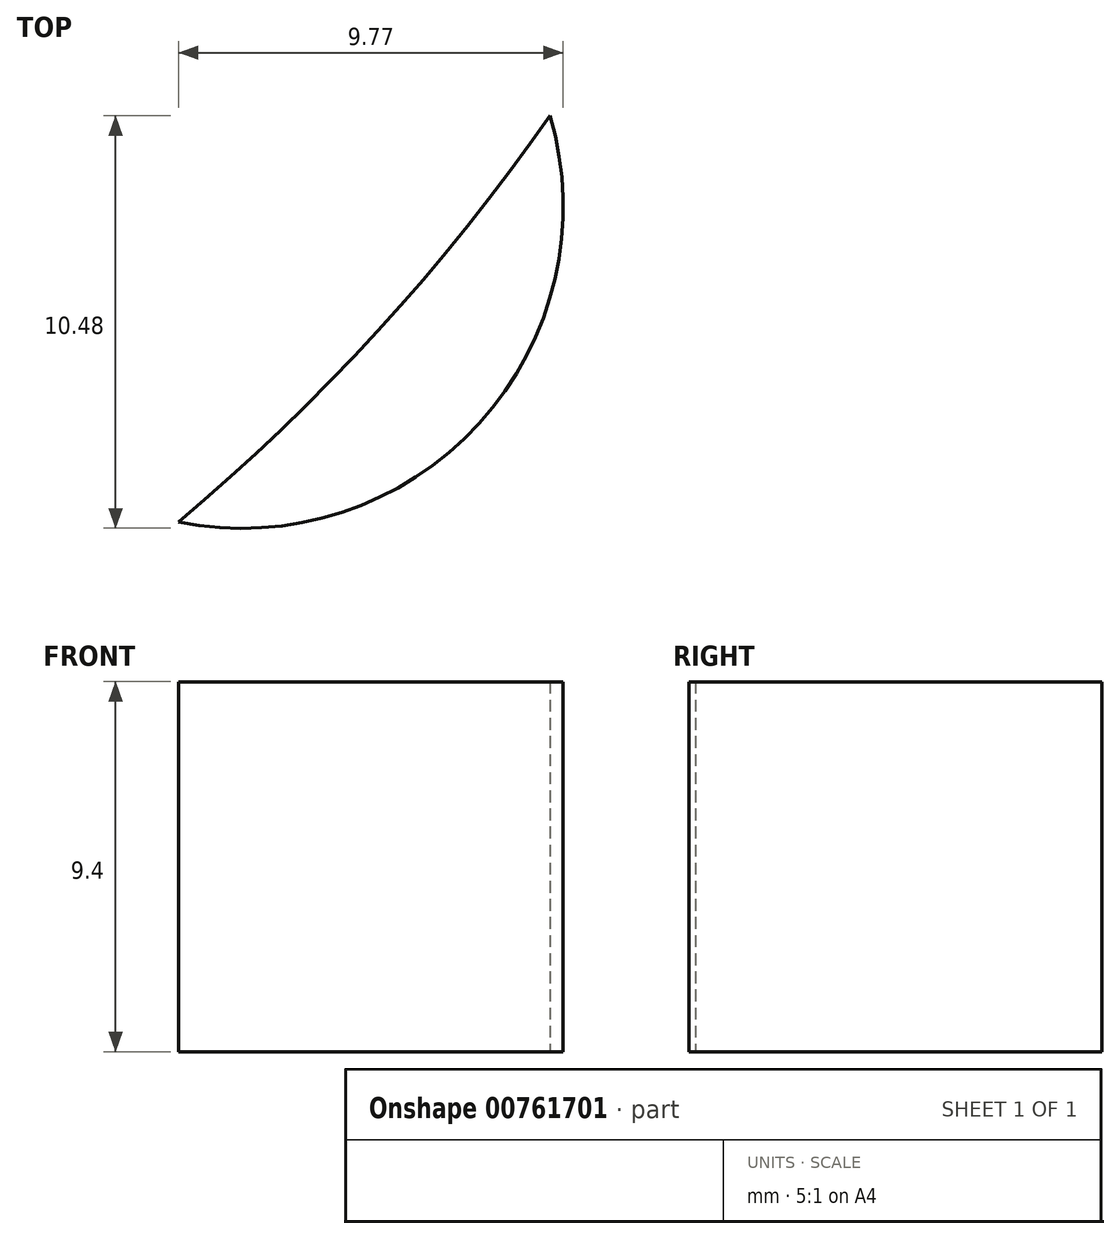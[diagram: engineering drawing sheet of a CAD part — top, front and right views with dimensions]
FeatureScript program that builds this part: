
annotation { "Feature Type Name" : "Feature", "Feature Type Description" : "" }
export const myFeature = defineFeature(function(context is Context, id is Id, definition is map)
    precondition{}
    {
        {
            var Q0;
            Q0=qCreatedBy(makeId("Top.planeOp"),FACE);
            var sketch = newSketch(context, id + "F0", { "sketchPlane" : qUnion([Q0])});
            skArc(sketch, "E0", {"start": v(4.93, 13.7) * mm, "mid": v(9.99, 18.55) * mm, "end": v(14.37, 24.02) * mm});
            skArc(sketch, "E1", {"start": v(4.93, 13.7) * mm, "mid": v(12.56, 16.2) * mm, "end": v(14.37, 24.02) * mm});
            skSolve(sketch);
        }
        {
            var Q0;
            Q0=makeQuery(id+"F0.imprint","IMPRINT",FACE,{"disambiguationData":[TD([[makeQuery(id+"F0.imprint","IMPRINT",EDGE,{"derivedFrom":sQuery(id+"F0.wireOp",EDGE,"RSaEAb7V-mC8l-hXbN-79xi-CSJ5uPoV2WZU")}),1.0]])]});
            var Q1;
            Q1=makeQuery(id+"F0.imprint","IMPRINT",FACE,{"disambiguationData":[TD([[makeQuery(id+"F0.imprint","IMPRINT",EDGE,{"derivedFrom":sQuery(id+"F0.wireOp",EDGE,"E0")}),-1.0]])]});
            extrude(context, id + "F1", {"entities" : qUnion([Q0, Q1]), "depth" : 9.4 * mm, "offsetDistance" : 25.4 * mm});
        }
    });
